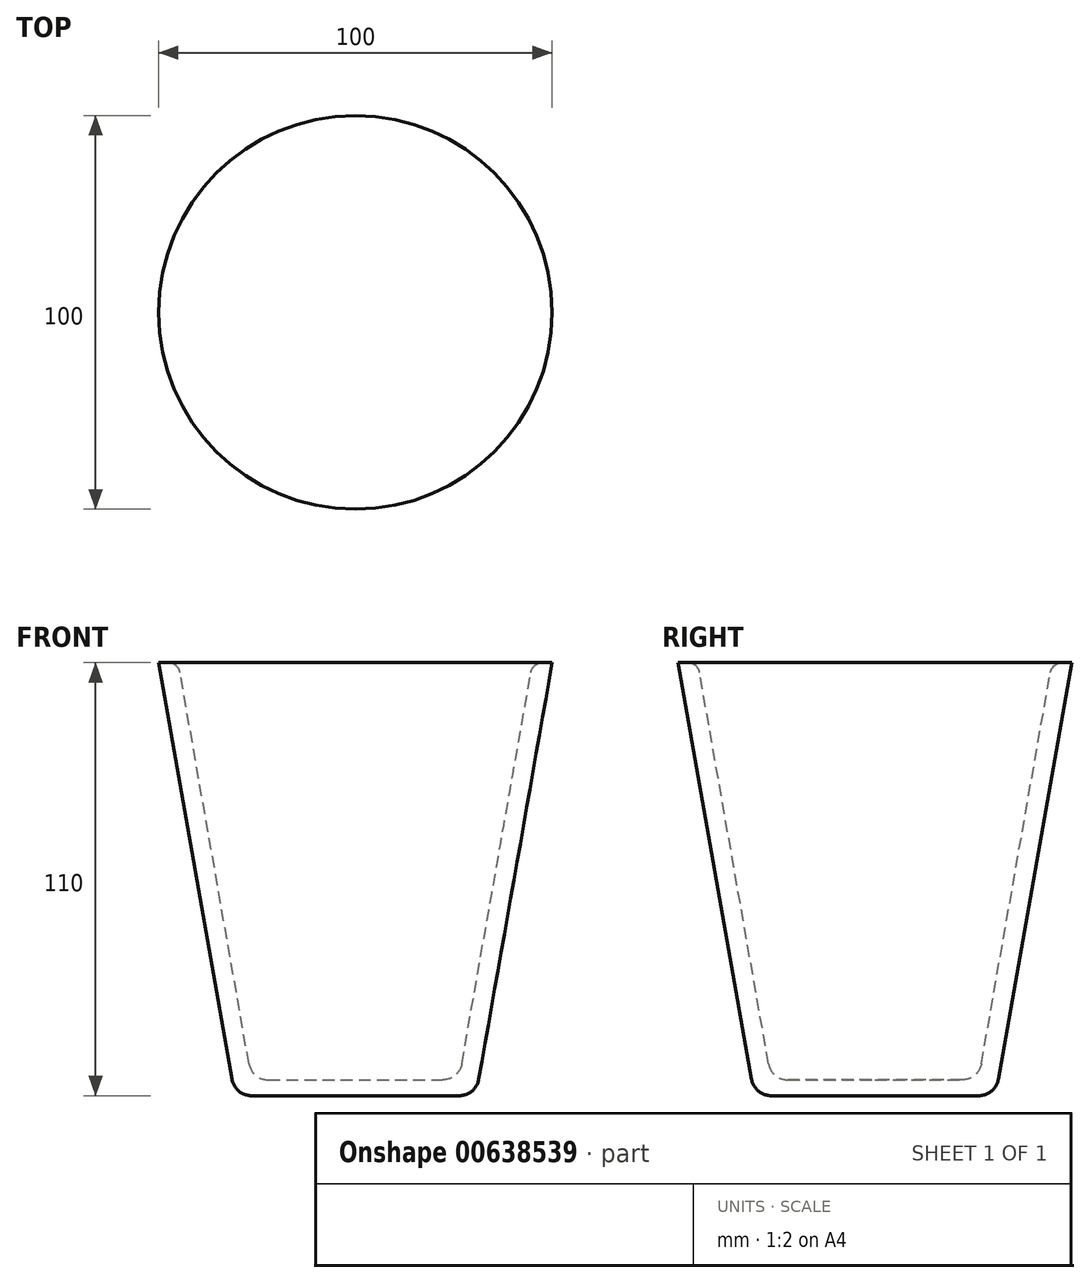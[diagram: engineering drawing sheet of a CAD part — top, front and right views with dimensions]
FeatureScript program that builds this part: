
annotation { "Feature Type Name" : "Feature", "Feature Type Description" : "" }
export const myFeature = defineFeature(function(context is Context, id is Id, definition is map)
    precondition{}
    {
        {
            var Q0;
            Q0=qCreatedBy(makeId("Front.planeOp"),FACE);
            var sketch = newSketch(context, id + "F0", { "sketchPlane" : qUnion([Q0])});
            skLineSegment(sketch, "E0", {"start": v(0, 0) * mm, "end": v(-30.6, 0) * mm});
            skLineSegment(sketch, "E1", {"start": v(-30.6, 0) * mm, "end": v(-50, 110) * mm});
            skLineSegment(sketch, "E2", {"start": v(-50, 110) * mm, "end": v(-45, 110) * mm});
            skLineSegment(sketch, "E3", {"start": v(-45, 110) * mm, "end": v(-26.3, 4) * mm});
            skLineSegment(sketch, "E4", {"start": v(-26.3, 4) * mm, "end": v(0, 4) * mm});
            skLineSegment(sketch, "E5", {"start": v(0, 4) * mm, "end": v(0, 0) * mm});
            skSolve(sketch);
        }
        {
            var Q0;
            Q0=makeQuery(id+"F0.imprint","IMPRINT",FACE,{"disambiguationData":[TD([[makeQuery(id+"F0.imprint","IMPRINT",EDGE,{"derivedFrom":sQuery(id+"F0.wireOp",EDGE,"E0")}),-1.0]])]});
            var Q1;
            Q1=sQuery(id+"F0.wireOp",EDGE,"E5");
            revolve(context, id + "F1", {"entities" : qUnion([Q0]), "axis" : qUnion([Q1]), "revolveType" : RevolveType.FULL});
        }
        {
            var Q0;
            Q0=makeQuery(id+"F1.opRevolve","SWEPT_EDGE",EDGE,{"disambiguationData":[OSD([sQuery(id+"F0.wireOp",EDGE,"E3"),sQuery(id+"F0.wireOp",EDGE,"E4")])]});
            fillet(context, id + "F2", {"entities" : qUnion([Q0]), "radius" : 5 * mm, "tangentPropagation" : true, "allowEdgeOverflow" : false});
        }
        {
            var Q0;
            Q0=makeQuery(id+"F1.opRevolve","SWEPT_EDGE",EDGE,{"disambiguationData":[OSD([sQuery(id+"F0.wireOp",EDGE,"E0"),sQuery(id+"F0.wireOp",EDGE,"E1")])]});
            fillet(context, id + "F3", {"entities" : qUnion([Q0]), "radius" : 5 * mm, "tangentPropagation" : true, "allowEdgeOverflow" : false});
        }
        {
            var Q0;
            Q0=makeQuery(id+"F1.opRevolve","SWEPT_EDGE",EDGE,{"disambiguationData":[OSD([sQuery(id+"F0.wireOp",EDGE,"E2"),sQuery(id+"F0.wireOp",EDGE,"E3")])]});
            fillet(context, id + "F4", {"entities" : qUnion([Q0]), "radius" : 3 * mm, "tangentPropagation" : true, "allowEdgeOverflow" : false});
        }
    });
